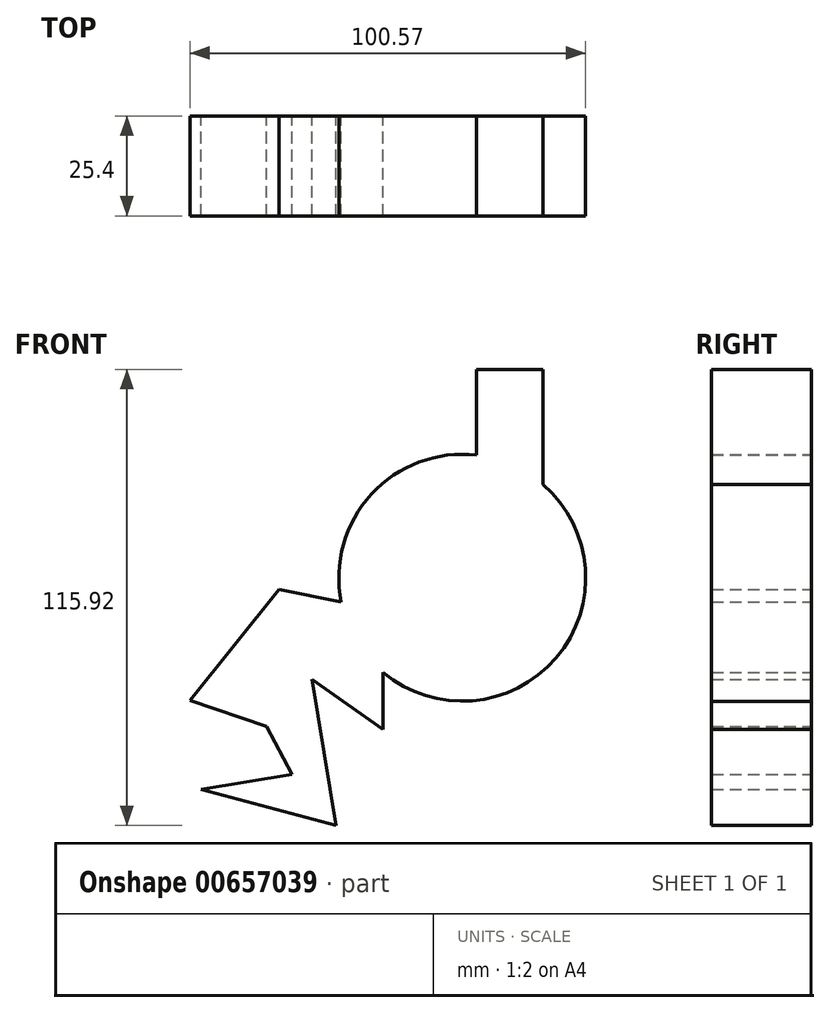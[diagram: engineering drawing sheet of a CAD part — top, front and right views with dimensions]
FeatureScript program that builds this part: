
annotation { "Feature Type Name" : "Feature", "Feature Type Description" : "" }
export const myFeature = defineFeature(function(context is Context, id is Id, definition is map)
    precondition{}
    {
        {
            var Q0;
            Q0=qCreatedBy(makeId("Front.planeOp"),FACE);
            var sketch = newSketch(context, id + "F0", { "sketchPlane" : qUnion([Q0])});
            skLineSegment(sketch, "E0", {"start": v(-180.06, -29.45) * mm, "end": v(-199.53, -22.81) * mm});
            skLineSegment(sketch, "E1", {"start": v(-199.53, -22.81) * mm, "end": v(-176.82, 5.37) * mm});
            skLineSegment(sketch, "E2", {"start": v(-176.82, 5.37) * mm, "end": v(-150.5, 0) * mm});
            skLineSegment(sketch, "E3", {"start": v(-150.5, 0) * mm, "end": v(-150.5, -30.18) * mm});
            skLineSegment(sketch, "E4", {"start": v(-150.5, -30.18) * mm, "end": v(-168.53, -17.47) * mm});
            skLineSegment(sketch, "E5", {"start": v(-168.53, -17.47) * mm, "end": v(-162.4, -54.63) * mm});
            skLineSegment(sketch, "E6", {"start": v(-162.4, -54.63) * mm, "end": v(-196.64, -45.41) * mm});
            skLineSegment(sketch, "E7", {"start": v(-196.64, -45.41) * mm, "end": v(-173.57, -41.63) * mm});
            skLineSegment(sketch, "E8", {"start": v(-173.57, -41.63) * mm, "end": v(-180.06, -29.45) * mm});
            skSolve(sketch);
        }
        {
            var Q0;
            Q0 = qSketchRegion(id + "F0", true);
            extrude(context, id + "F1", {"entities" : qUnion([Q0]), "depth" : 25.4 * mm, "offsetDistance" : 25.4 * mm});
        }
        {
            var Q0;
            Q0=qCreatedBy(makeId("Front.planeOp"),FACE);
            var sketch = newSketch(context, id + "F2", { "sketchPlane" : qUnion([Q0])});
            skLineSegment(sketch, "E9", {"start": v(-154.47, 29.13) * mm, "end": v(-115.53, 21.26) * mm});
            skLineSegment(sketch, "E10.bottom", {"start": v(-126.7, 61.3) * mm, "end": v(-109.77, 61.3) * mm});
            skLineSegment(sketch, "E10.top", {"start": v(-126.7, 24) * mm, "end": v(-109.77, 24) * mm});
            skLineSegment(sketch, "E10.left", {"start": v(-126.7, 61.3) * mm, "end": v(-126.7, 24) * mm});
            skLineSegment(sketch, "E10.right", {"start": v(-109.77, 61.3) * mm, "end": v(-109.77, 24) * mm});
            skCircle(sketch, "E11", {"center": v(-130.31, 8.34) * mm, "radius": 31.36 * mm});
            skArc(sketch, "E12", {"start": v(-78.4, 23.33) * mm, "mid": v(-40.41, 76.08) * mm, "end": v(-104.72, 66.56) * mm});
            skSolve(sketch);
        }
        {
            var Q0;
            Q0 = qSketchRegion(id + "F2", true);
            extrude(context, id + "F3", {"entities" : qUnion([Q0]), "operationType" : NewBodyOperationType.ADD, "depth" : 25.4 * mm, "offsetDistance" : 25.4 * mm});
        }
    });
